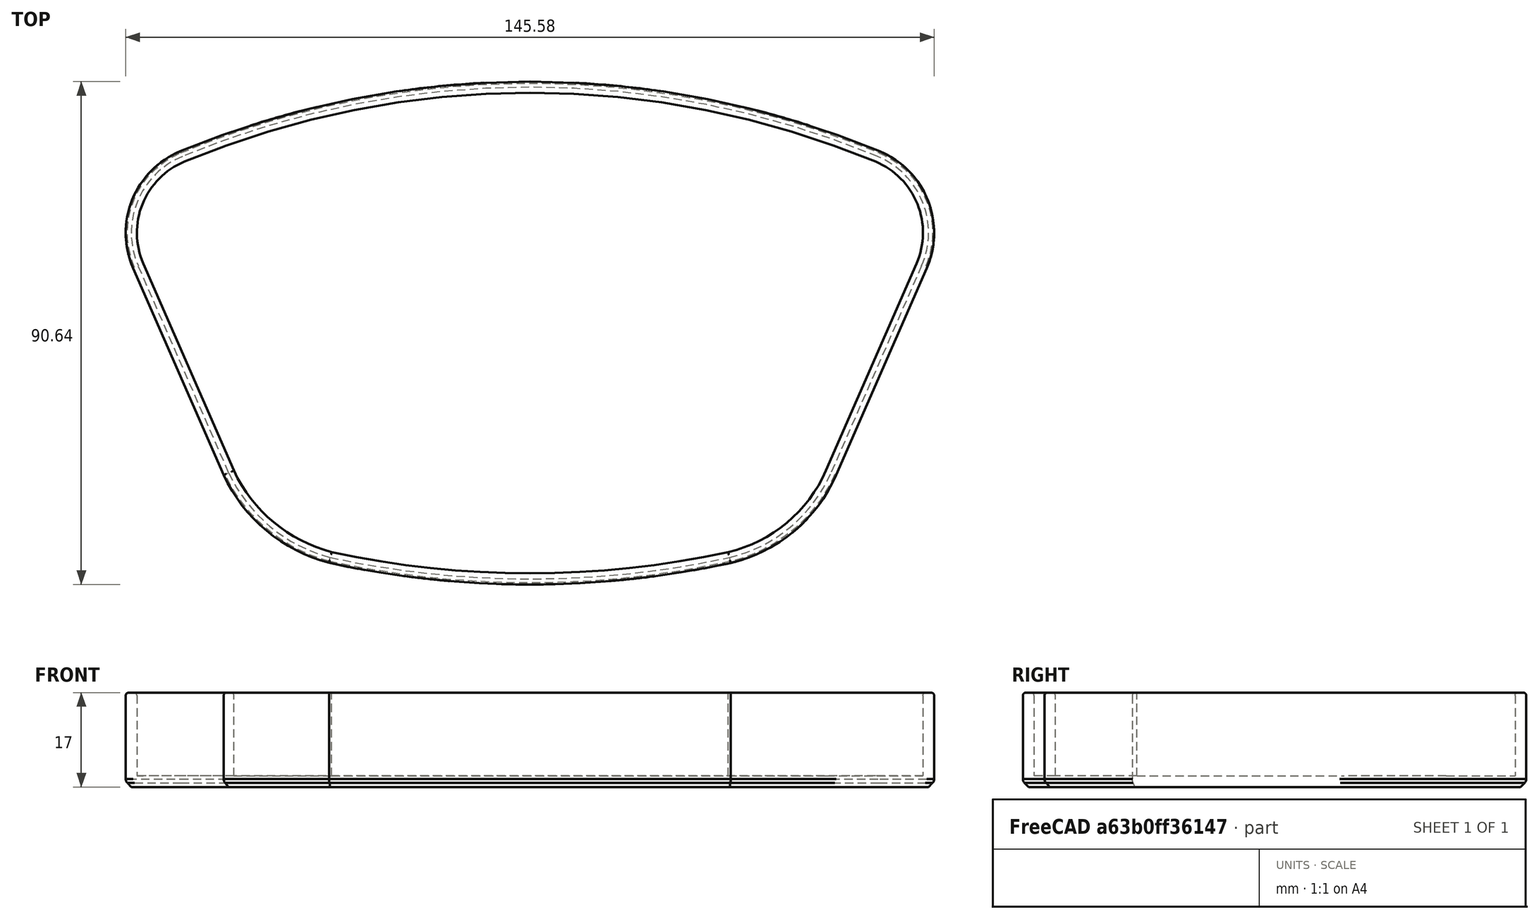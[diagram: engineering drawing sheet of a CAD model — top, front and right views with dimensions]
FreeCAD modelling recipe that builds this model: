
FCSTD DOCUMENT  (FreeCAD 0.19R24054 (Git))
Label: mixer cover cap
License: All rights reserved
LicenseURL: http://en.wikipedia.org/wiki/All_rights_reserved
objects: PartDesign::Fillet×2, Image::ImagePlane×1, Sketcher::SketchObject×1, PartDesign::Pad×1, PartDesign::Thickness×1, PartDesign::Chamfer×1, PartDesign::Body×1
note: 12 computed .brp shape members not serialized (recipe doc carries the construction recipe); baked Part::Feature solids carry a one-line shape summary decoded from their .brp

FEATURE [Image::ImagePlane] ImagePlane
  Placement = pos=(0,0,-0.01) rot=(0,0,1;0.017453rad)
  XSize = 166.715
  YSize = 114.804
FEATURE [Sketcher::SketchObject] Sketch
  FullyConstrained = false
  MapMode = 5
  Support = -> [XY_Plane]
  sketch-geometry (14):
    g0: ArcOfCircle CenterX=29.8122 CenterY=-17.0882 CenterZ=0 NormalX=0 NormalY=0 NormalZ=1 AngleXU=0 Radius=25.6574 StartAngle=4.94425 EndAngle=5.87116
    g1: ArcOfCircle CenterX=-28.8785 CenterY=-15.9691 CenterZ=0 NormalX=0 NormalY=0 NormalZ=1 AngleXU=0 Radius=26.9689 StartAngle=3.57778 EndAngle=4.45637
    g2: ArcOfCircle CenterX=2.14e-14 CenterY=121.961 CenterZ=0 NormalX=0 NormalY=0 NormalZ=1 AngleXU=0 Radius=167.862 StartAngle=4.49803 EndAngle=4.92675
    g3: GeomPoint X=69.6263 Y=9.9427 Z=0
    g4: GeomPoint X=-69.6263 Y=9.9427 Z=0
    g5: GeomPoint X=62.2291 Y=28.3265 Z=0
    g6: GeomPoint X=-62.2291 Y=28.3265 Z=0
    g7: LineSegment StartX=53.3223 StartY=-27.363 StartZ=0 EndX=69.6263 EndY=9.9427 EndZ=0
    g8: LineSegment StartX=-53.3223 StartY=-27.363 StartZ=0 EndX=-69.6263 EndY=9.9427 EndZ=0
    g9: ArcOfCircle CenterX=56.903 CenterY=15.5033 CenterZ=0 NormalX=0 NormalY=0 NormalZ=1 AngleXU=0 Radius=13.8854 StartAngle=5.87116 EndAngle=7.46031
    g10: ArcOfCircle CenterX=-56.903 CenterY=15.5033 CenterZ=0 NormalX=0 NormalY=0 NormalZ=1 AngleXU=0 Radius=13.8854 StartAngle=1.96446 EndAngle=3.55361
    g11: ArcOfCircle CenterX=-1.26e-14 CenterY=-121.497 CenterZ=0 NormalX=0 NormalY=0 NormalZ=1 AngleXU=0 Radius=162.233 StartAngle=1.17713 EndAngle=1.96446
    g12: GeomPoint X=0 Y=40.736 Z=0
    g13: GeomPoint X=0 Y=42.736 Z=0
  constraints (26):
    c: DistanceY(g0) = -17.0882
    c: Symmetric(g1,g0,g-2)
    c: Coincident(g2,g1)
    c: Coincident(g2,g0)
    c: DistanceX(g0) = 35.7078
    c: DistanceY(g0) = -42.059
    c: Symmetric(g5,g6,g-2)
    c: Coincident(g7,g0)
    c: Coincident(g8,g1)
    c: Coincident(g8,g4)
    c: Coincident(g7,g3)
    c: Coincident(g9,g5)
    c: Coincident(g10,g6)
    c: PointOnObject(g12,g11)
    c: PointOnObject(g13,g-2)
    c: PointOnObject(g12,g-2)
    c: DistanceY(g12,g13) = 2
    c: Tangent(g9,g7) = -1.5708
    c: Symmetric(g7,g8,g-2)
    c: Coincident(g10,g8)
    c: Symmetric(g10,g9,g-2)
    c: DistanceX(g7) = 69.6263
    c: DistanceY(g7) = 9.9427
    c: Tangent(g9,g11) = -1.5708
    c: Coincident(g11,g10)
    c: DistanceY(g13) = 42.736
FEATURE [PartDesign::Pad] Pad
  Direction = (1,1,1)
  Length = 15
  Length2 = 100
  Profile = -> Sketch
  Refine = true
  Type = 0
FEATURE [PartDesign::Thickness] Thickness
  Base = -> Pad [Face10]
  BaseFeature = -> Pad
  Intersection = false
  Join = 1
  Mode = 0
  Refine = true
  SupportTransform = false
  Value = 2
FEATURE [PartDesign::Fillet] Fillet
  Base = -> Thickness [Face10]
  BaseFeature = -> Thickness
  Radius = 0.5
  Refine = true
  SupportTransform = false
FEATURE [PartDesign::Chamfer] Chamfer
  Angle = 45
  Base = -> Fillet [Edge77]
  BaseFeature = -> Fillet
  ChamferType = 0
  FlipDirection = false
  Refine = true
  Size = 1
  Size2 = 1
  SupportTransform = false
FEATURE [PartDesign::Fillet] Fillet001
  Base = -> Chamfer [Edge56]
  BaseFeature = -> Chamfer
  Radius = 1
  Refine = true
  SupportTransform = false
FEATURE [PartDesign::Body] Body
  Group = -> [Sketch,Pad,Thickness,Fillet,Chamfer,Fillet001]
  Origin = -> Origin
  Tip = -> Fillet001
